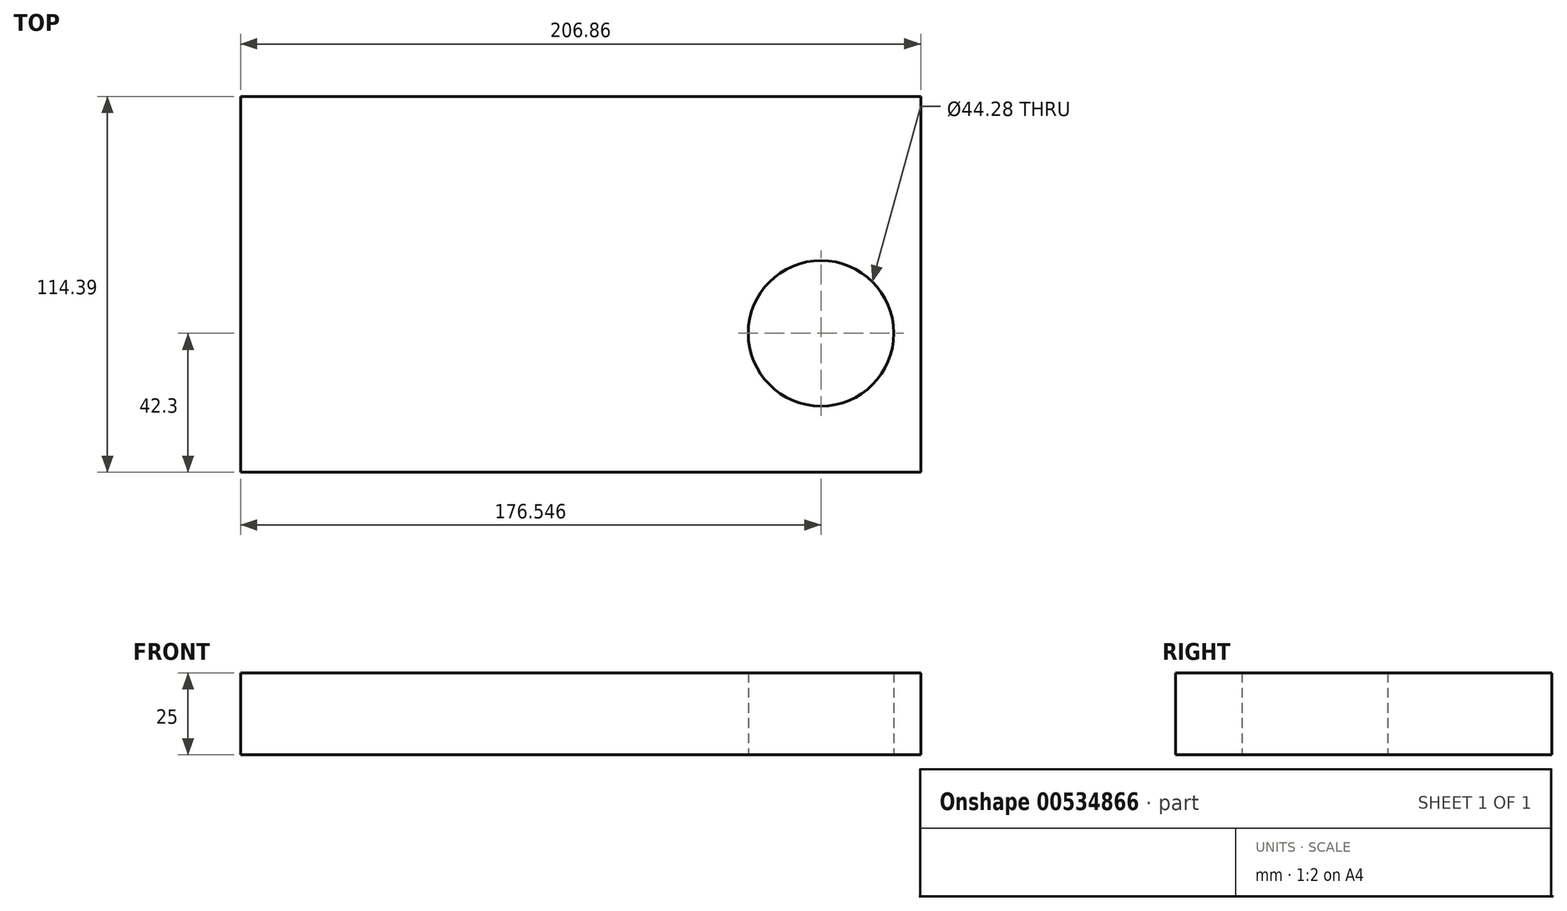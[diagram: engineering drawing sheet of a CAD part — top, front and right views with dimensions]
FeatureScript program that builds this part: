
annotation { "Feature Type Name" : "Feature", "Feature Type Description" : "" }
export const myFeature = defineFeature(function(context is Context, id is Id, definition is map)
    precondition{}
    {
        {
            var Q0;
            Q0=qCreatedBy(makeId("Top.planeOp"),FACE);
            var sketch = newSketch(context, id + "F0", { "sketchPlane" : qUnion([Q0])});
            skLineSegment(sketch, "E0.bottom", {"start": v(164.99, 71.75) * mm, "end": v(-41.87, 71.75) * mm});
            skLineSegment(sketch, "E0.top", {"start": v(164.99, -42.64) * mm, "end": v(-41.87, -42.64) * mm});
            skLineSegment(sketch, "E0.left", {"start": v(164.99, 71.75) * mm, "end": v(164.99, -42.64) * mm});
            skLineSegment(sketch, "E0.right", {"start": v(-41.87, 71.75) * mm, "end": v(-41.87, -42.64) * mm});
            skCircle(sketch, "E1", {"center": v(134.68, -0.34) * mm, "radius": 22.14 * mm});
            skSolve(sketch);
        }
        {
            var Q0;
            Q0 = qSketchRegion(id + "F0", true);
            extrude(context, id + "F1", {"entities" : qUnion([Q0]), "depth" : 25 * mm, "offsetDistance" : 25 * mm});
        }
    });
